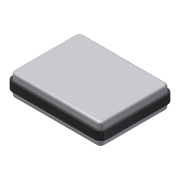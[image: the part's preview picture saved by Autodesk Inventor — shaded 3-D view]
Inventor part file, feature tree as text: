
AUTODESK INVENTOR PART (.ipt)
format: ipt  version: 2013 (Build 170138000, 138)  size: 134,656 bytes
history: native  units: in
note: dims shown in document units (in); Inventor stores cm internally (conversion verified against a paired STEP export)
features: extrude x2, fillet x2, sketch x2, projected_geometry x1
ambient origin geometry x8: Origin, YZ Plane, XZ Plane, XY Plane, X Axis, Y Axis, Z Axis, Center Point
bodies: Solid1 (feature_tree), Solid2 (feature_tree)
feature tree (7):
  extrude  "Extrusion1"  Depth=4.15in
  fillet  "Fillet1"  Radius=1.3in
  fillet  "Fillet2"  Radius=0.25in
  extrude  "Extrusion2"  Depth=0.125in
  sketch  "Sketch2"  dims[d0=5.45in d1=4.15in d2=1.3in d3=0.0in d4=0.25in]
  sketch  "Sketch3"  dims[d5=0.125in d6=0.125in d7=0.5in d8=0.0in]
  projected_geometry  "Project Cut Edges1"
